# Revit family: R 402 (a)
name_source: partatom
category: Equipement spécialisé
revit_build: Autodesk Revit LT 2015 (Build: 20140606_1530(x64)
units: mm (PartAtom-declared; Revit-internal decimal feet)

## types (8) — shared parameters
Apparent Power = 0 VA
Depth Coupe-Légumes = 300 mm
Depth Cutter = 305 mm
Depth Electrique connexion Coupe-Légumes = 40 mm  [stored 0.131234 ft]
Depth Electrique connnexion Cutter = 46 mm
Description = COMBINES
Fabricant = ROBOT COUPE
Height Coupe-Légumes = 590 mm
Height Cutter = 462 mm
Modèle = R 402
UP Depth Coupe-Légumes = 373 mm
UP Height Coupe-Légumes = 685 mm
UP Width Coupe-Légumes = 490 mm
URL = www.robot-coupe.com
Width Coupe-Légumes = 422 mm
Width Cutter = 225 mm  [stored 0.738189 ft]
water = Connector
zero-valued in all types: Cold water supply, Cold water supply height, Used water, Waste water height

## per-type parameters (varying)
| type | Amps | Cycle | HP | Phase | Speeds (Rpm) | Volts | Watts | Weight |
| R 402   230/50/1 | 5.4 A | 50 Hz |  | 1 | 500 and 1500 | 230 V | 750 W | 20.5 kg |
| R 402   120/60/1 | 9 A | 60 Hz |  | 1 | 500 and 1500 | 120 V | 750 W | 20.5 kg |
| R 402   220/60/3 | 3 A | 60 Hz |  | 3 | 750 and 1500 | 220 V | 750 W | 20.5 kg |
| R 402   220-240/50/1 | 5.4 A | 50 Hz |  | 1 | 500 and 1500 | 220 V | 750 W | 20.5 kg |
| R 402 USA   120/60/1 | 9 A | 60 Hz | 2 | 1 | 600 and 1800 | 120 V | 0 W | 49 lbs |
| R 402   230/50/3 | 2.8 A | 50 Hz |  | 3 | 750 and 1500 | 230 V | 750 W | 20.5 kg |
| R 402   380/60/3 | 1.6 A | 60 Hz |  | 3 | 750 and 1500 | 380 V | 750 W | 20.5 kg |
| R 402   400/50/3 | 1.6 A | 50 Hz |  | 3 | 750 and 1500 | 400 V | 750 W | 20.5 kg |

note: [stored X ft] marks values corroborated as IEEE doubles in the binary element streams (Revit-internal decimal feet)

## geometry (parser evidence)
native form markers: Blend x79, Sweep x4
no freeform markers — native parametric forms only
